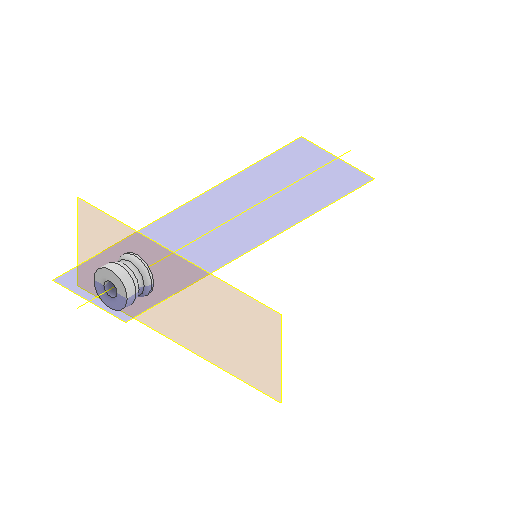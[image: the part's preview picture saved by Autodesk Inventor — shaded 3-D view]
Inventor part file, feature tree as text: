
AUTODESK INVENTOR PART (.ipt)
format: ipt  version: 2022 (Build 260153000, 153)  size: 136,704 bytes
history: native  units: mm
features: other x8, plane x2, sketch x2, extrude x1, revolve x1, fillet x1, reference x1
ambient origin geometry x8: Origin, YZ Plane, XZ Plane, XY Plane, X Axis, Y Axis, Z Axis, Center Point
bodies: Solid1 (feature_tree)
feature tree (16):
  plane  "Work Plane1"
  extrude  "Extrusion1"  TaperAngle=90.0deg  [1 undecoded]
  plane  "Work Plane2"
  other  "Work Axis1"
  revolve  "Revolution1"  [1 undecoded]
  fillet  "Fillet1"  [1 undecoded]
  sketch  "Sketch1"  dims[d0=8.0mm d1=0.0mm d2=90.0deg]
  reference  "Reference3"
  sketch  "Sketch2"  dims[d3=2.0mm d4=4.0mm]
  other  "<userpath>\Documents\GitHub\Guinardia\INVENTOR\Assembly_Guinardia_V1.iam"
  other  "Assembly_Guinardia_V1.iam"
  other  "20_Cube_Insert_Lightsheet_FEPTube_Rotating_hollomotor_v0:1"
  other  "<userpath>\Documents\Inventor\Guinardia\INVENTOR\Assembly_Guinardia_V0.iam"
  other  "Assembly_Guinardia_V0.iam"
  other  "10_Wellplate_base:1"
  other  "00_NEMA8:1"
note: 3 required parameter values undecoded (feature->parameter linkage not recoverable at this tier; creation-order binding heuristic only, values carry confidence <= 0.55)